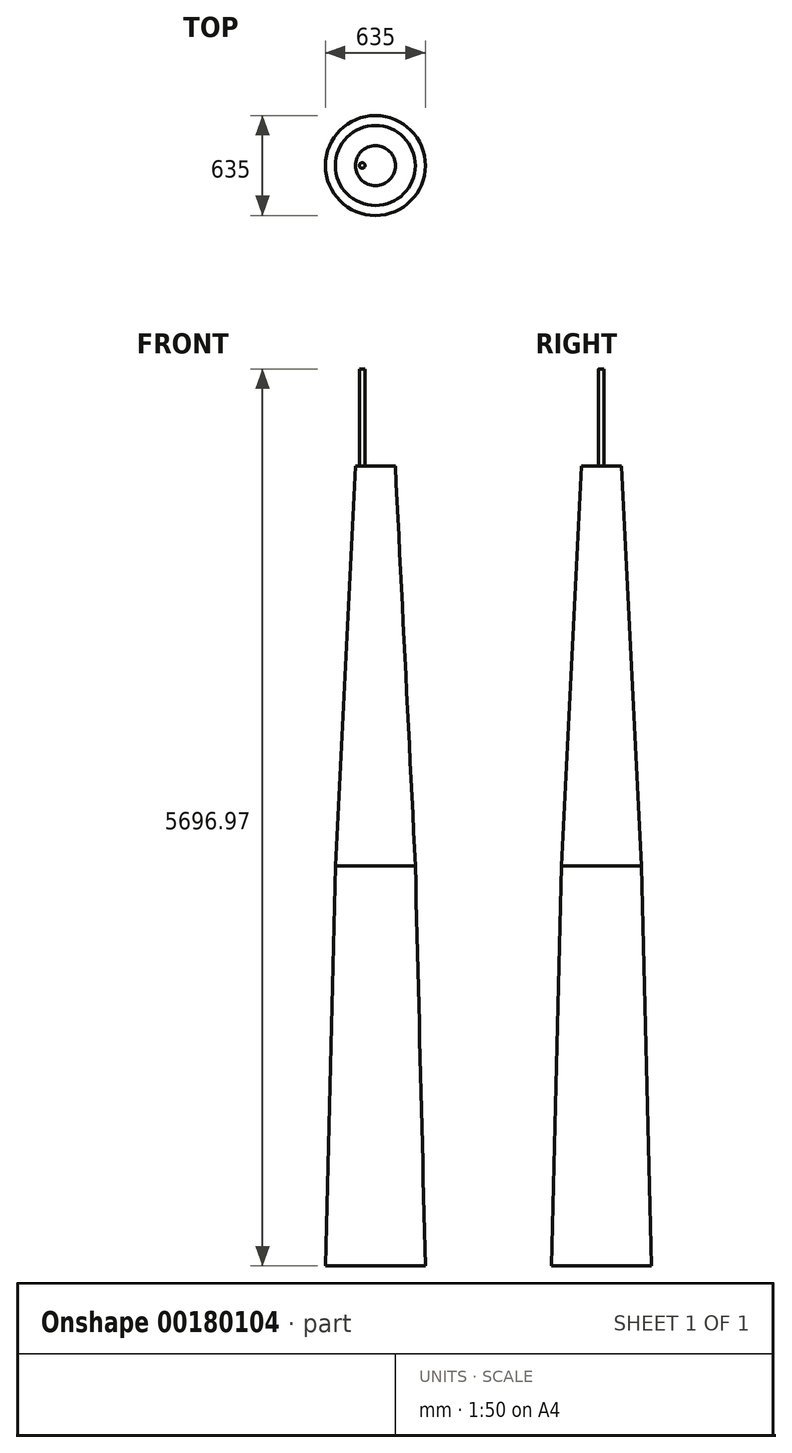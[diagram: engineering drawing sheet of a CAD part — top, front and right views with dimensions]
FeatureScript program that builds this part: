
annotation { "Feature Type Name" : "Feature", "Feature Type Description" : "" }
export const myFeature = defineFeature(function(context is Context, id is Id, definition is map)
    precondition{}
    {
        {
            var Q0;
            Q0=qCreatedBy(makeId("Top.planeOp"),FACE);
            var sketch = newSketch(context, id + "F0", { "sketchPlane" : qUnion([Q0])});
            skCircle(sketch, "E0", {"center": v(0, 0) * mm, "radius": 317.5 * mm});
            skSolve(sketch);
        }
        {
            var Q0;
            Q0=makeQuery(id+"F0.imprint","IMPRINT",FACE,{"disambiguationData":[TD([[makeQuery(id+"F0.imprint","IMPRINT",EDGE,{"derivedFrom":sQuery(id+"F0.wireOp",EDGE,"E0")}),1.0]])]});
            cPlane(context, id + "F1", {"entities" : qUnion([Q0]), "cplaneType" : CPlaneType.OFFSET, "offset" : 2540 * mm, "width" : 152.4 * mm, "height" : 152.4 * mm});
        }
        {
            var Q0;
            Q0=qCreatedBy(id+"F1.planeOp",FACE);
            var sketch = newSketch(context, id + "F2", { "sketchPlane" : qUnion([Q0])});
            skCircle(sketch, "E1", {"center": v(0, 0) * mm, "radius": 254 * mm});
            skSolve(sketch);
        }
        {
            var Q0;
            Q0=makeQuery(id+"F2.imprint","IMPRINT",FACE,{"disambiguationData":[TD([[makeQuery(id+"F2.imprint","IMPRINT",EDGE,{"derivedFrom":sQuery(id+"F2.wireOp",EDGE,"E1")}),1.0]])]});
            cPlane(context, id + "F3", {"entities" : qUnion([Q0]), "cplaneType" : CPlaneType.OFFSET, "offset" : 2540 * mm, "width" : 152.4 * mm, "height" : 152.4 * mm});
        }
        {
            var Q0;
            Q0=qCreatedBy(id+"F3.planeOp",FACE);
            var sketch = newSketch(context, id + "F4", { "sketchPlane" : qUnion([Q0])});
            skCircle(sketch, "E2", {"center": v(0, 0) * mm, "radius": 127 * mm});
            skPoint(sketch, "E3", {"position": v(-127, 0) * mm});
            skPoint(sketch, "E4", {"position": v(0, -127) * mm});
            skPoint(sketch, "E5", {"position": v(0, 127) * mm});
            skPoint(sketch, "E6", {"position": v(127, 0) * mm});
            skSolve(sketch);
        }
        {
            var Q0;
            Q0=makeQuery(id+"F0.imprint","IMPRINT",FACE,{"disambiguationData":[TD([[makeQuery(id+"F0.imprint","IMPRINT",EDGE,{"derivedFrom":sQuery(id+"F0.wireOp",EDGE,"E0")}),1.0]])]});
            var Q1;
            Q1=makeQuery(id+"F2.imprint","IMPRINT",FACE,{"disambiguationData":[TD([[makeQuery(id+"F2.imprint","IMPRINT",EDGE,{"derivedFrom":sQuery(id+"F2.wireOp",EDGE,"E1")}),1.0]])]});
            loft(context, id + "F5", {"sheetProfilesArray" : [{ "sheetProfileEntities" : qUnion([Q0]) }, { "sheetProfileEntities" : qUnion([Q1]) }]});
        }
        {
            var Q1;
            Q1=makeQuery(id+"F5.opLoft","CAP_FACE",FACE,{"disambiguationData":[OSD([makeQuery(id+"F2.imprint","IMPRINT",FACE,{"disambiguationData":[TD([[makeQuery(id+"F2.imprint","IMPRINT",EDGE,{"derivedFrom":sQuery(id+"F2.wireOp",EDGE,"E1")}),1.0]])]})])],"isStart":true});
            var Q2;
            Q2=makeQuery(id+"F4.imprint","IMPRINT",FACE,{"disambiguationData":[TD([[makeQuery(id+"F4.imprint","IMPRINT",EDGE,{"derivedFrom":sQuery(id+"F4.wireOp",EDGE,"E2")}),1.0]])]});
            loft(context, id + "F6", {"operationType" : NewBodyOperationType.ADD, "sheetProfilesArray" : [{ "sheetProfileEntities" : qUnion([Q1]) }, { "sheetProfileEntities" : qUnion([Q2]) }]});
        }
        {
            var Q0;
            Q0=qCreatedBy(makeId("Front.planeOp"),FACE);
            var sketch = newSketch(context, id + "F7", { "sketchPlane" : qUnion([Q0])});
            skLineSegment(sketch, "E7.bottom", {"start": v(0, 5667.8) * mm, "end": v(0, 5667.8) * mm});
            skLineSegment(sketch, "E7.top", {"start": v(0, 5058.57) * mm, "end": v(0, 5058.57) * mm});
            skLineSegment(sketch, "E8.bottom", {"start": v(-101.72, 5696.97) * mm, "end": v(-83.78, 5696.97) * mm});
            skLineSegment(sketch, "E8.top", {"start": v(-101.72, 5080.06) * mm, "end": v(-83.78, 5080.06) * mm});
            skLineSegment(sketch, "E8.left", {"start": v(-101.72, 5696.97) * mm, "end": v(-101.72, 5080.06) * mm});
            skLineSegment(sketch, "E8.right", {"start": v(-83.78, 5696.97) * mm, "end": v(-83.78, 5080.06) * mm});
            skSolve(sketch);
        }
        {
            var Q0;
            Q0=makeQuery(id+"F7.imprint","IMPRINT",FACE,{"disambiguationData":[TD([[makeQuery(id+"F7.imprint","IMPRINT",EDGE,{"derivedFrom":sQuery(id+"F7.wireOp",EDGE,"E8.bottom")}),-1.0]])]});
            var Q1;
            Q1=sQuery(id+"F7.wireOp",EDGE,"E8.right");
            revolve(context, id + "F8", {"entities" : qUnion([Q0]), "axis" : qUnion([Q1]), "revolveType" : RevolveType.FULL});
        }
        {
            var Q0;
            Q0=makeQuery(id+"F6.opLoft","CAP_FACE",FACE,{"disambiguationData":[OSD([makeQuery(id+"F4.imprint","IMPRINT",FACE,{"disambiguationData":[TD([[makeQuery(id+"F4.imprint","IMPRINT",EDGE,{"derivedFrom":sQuery(id+"F4.wireOp",EDGE,"E2")}),1.0]])]})])],"isStart":true});
            cPlane(context, id + "F9", {"entities" : qUnion([Q0]), "cplaneType" : CPlaneType.OFFSET, "offset" : 254 * mm, "width" : 152.4 * mm, "height" : 152.4 * mm});
        }
    });
